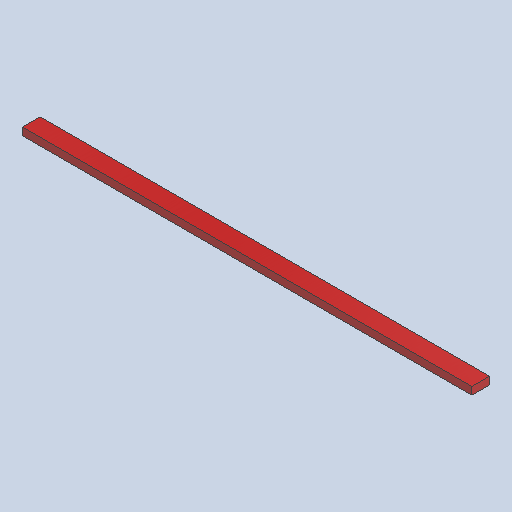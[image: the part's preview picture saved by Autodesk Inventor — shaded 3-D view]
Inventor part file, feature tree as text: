
AUTODESK INVENTOR PART (.ipt)
format: ipt  version: 2025.1 (Build 291241020, 241B)  size: 253,952 bytes
history: native  units: in
note: dims shown in document units (in); Inventor stores cm internally (conversion verified against a paired STEP export)
features: other x2, extrude x1, sketch x1
ambient origin geometry x8: Origin, YZ Plane, XZ Plane, XY Plane, X Axis, Y Axis, Z Axis, Center Point
bodies: Solid1 (feature_tree)
feature tree (4):
  extrude  "Extrusion1"  Depth=1.5in
  sketch  "Sketch1"  dims[d0=3.5in d1=1.5in d2=89.0in d3=0.0in]
  other  "Finish1"
  other  "Finish2"
